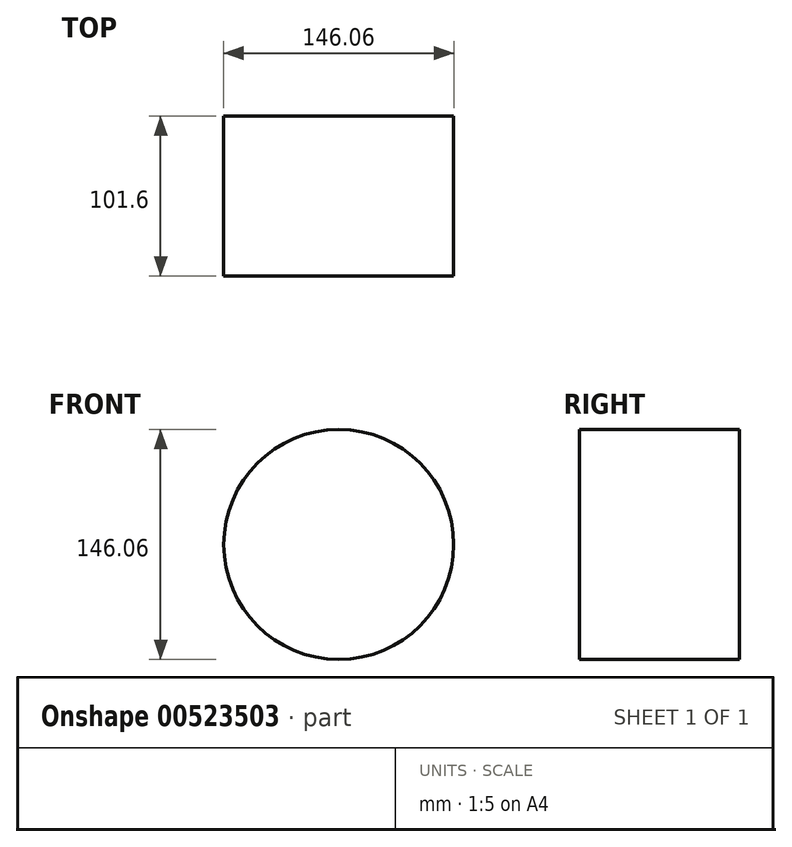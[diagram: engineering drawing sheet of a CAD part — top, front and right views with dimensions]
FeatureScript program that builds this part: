
annotation { "Feature Type Name" : "Feature", "Feature Type Description" : "" }
export const myFeature = defineFeature(function(context is Context, id is Id, definition is map)
    precondition{}
    {
        {
            var Q0;
            Q0=qCreatedBy(makeId("Front.planeOp"),FACE);
            var sketch = newSketch(context, id + "F0", { "sketchPlane" : qUnion([Q0])});
            skLineSegment(sketch, "E0", {"start": v(637.54, -320.04) * mm, "end": v(-637.54, -320.04) * mm});
            skLineSegment(sketch, "E1", {"start": v(-637.54, 320.04) * mm, "end": v(-637.54, -320.04) * mm});
            skLineSegment(sketch, "E2", {"start": v(637.54, 320.04) * mm, "end": v(637.54, -320.04) * mm});
            skLineSegment(sketch, "E3", {"start": v(637.54, 320.04) * mm, "end": v(-637.54, 320.04) * mm});
            skCircle(sketch, "E4", {"center": v(-476.25, 0) * mm, "radius": 73.03 * mm});
            skCircle(sketch, "E5", {"center": v(476.25, 0) * mm, "radius": 73.03 * mm});
            skLineSegment(sketch, "E6", {"start": v(-637.54, -320.04) * mm, "end": v(637.54, -320.04) * mm});
            skLineSegment(sketch, "E7", {"start": v(-637.54, 320.04) * mm, "end": v(637.54, 320.04) * mm});
            skCircle(sketch, "E8", {"center": v(266.5, 218.44) * mm, "radius": 61.34 * mm});
            skCircle(sketch, "E9", {"center": v(-305.37, 218.44) * mm, "radius": 61.34 * mm});
            skCircle(sketch, "E10", {"center": v(-305.37, -218.44) * mm, "radius": 61.34 * mm});
            skCircle(sketch, "E11", {"center": v(266.5, -218.44) * mm, "radius": 61.34 * mm});
            skLineSegment(sketch, "E12", {"start": v(-56.77, 127) * mm, "end": v(-56.77, -127) * mm});
            skLineSegment(sketch, "E13", {"start": v(-56.77, -127) * mm, "end": v(57.53, -127) * mm});
            skLineSegment(sketch, "E14", {"start": v(57.53, -127) * mm, "end": v(57.53, 127) * mm});
            skLineSegment(sketch, "E15", {"start": v(57.53, 127) * mm, "end": v(-56.77, 127) * mm});
            skSolve(sketch);
        }
        {
            var Q0;
            Q0=makeQuery(id+"F0.imprint","IMPRINT",FACE,{"disambiguationData":[TD([[makeQuery(id+"F0.imprint","IMPRINT",EDGE,{"derivedFrom":sQuery(id+"F0.wireOp",EDGE,"E4")}),1.0]])]});
            extrude(context, id + "F1", {"entities" : qUnion([Q0]), "depth" : 101.6 * mm, "offsetDistance" : 25.4 * mm});
        }
    });
